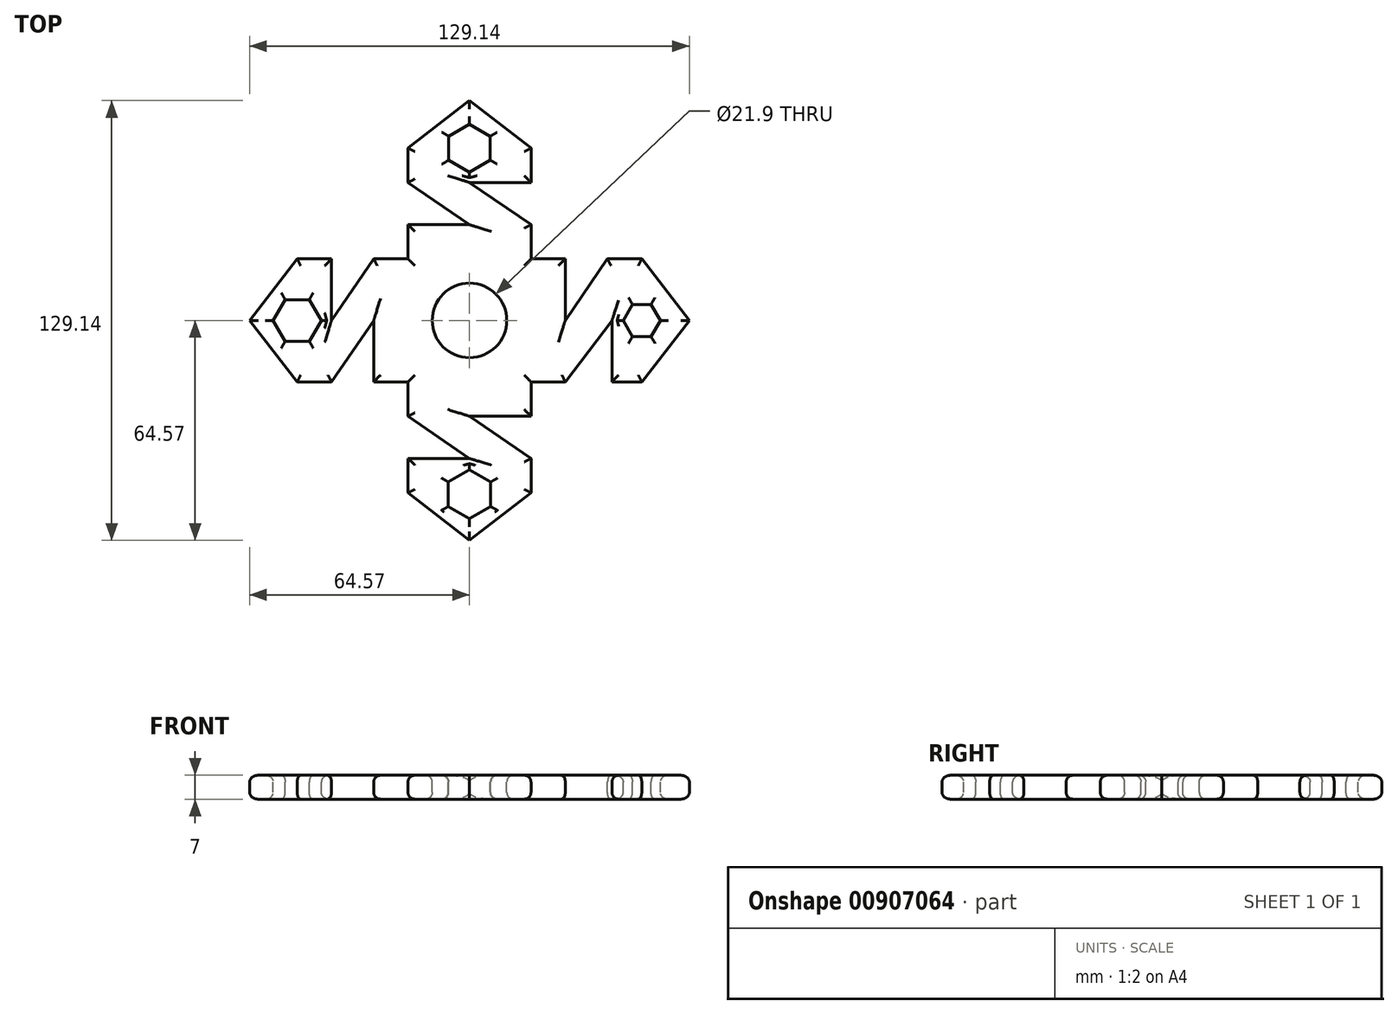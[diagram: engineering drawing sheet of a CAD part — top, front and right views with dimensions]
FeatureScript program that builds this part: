
annotation { "Feature Type Name" : "Feature", "Feature Type Description" : "" }
export const myFeature = defineFeature(function(context is Context, id is Id, definition is map)
    precondition{}
    {
        {
            var Q0;
            Q0=qCreatedBy(makeId("Top.planeOp"),FACE);
            var sketch = newSketch(context, id + "F0", { "sketchPlane" : qUnion([Q0])});
            skLineSegment(sketch, "E0", {"start": v(-18.07, 50.58) * mm, "end": v(0, 64.57) * mm});
            skLineSegment(sketch, "E1", {"start": v(18.07, 50.58) * mm, "end": v(0, 64.57) * mm});
            skLineSegment(sketch, "E2", {"start": v(0, 0) * mm, "end": v(-18.07, 18.07) * mm});
            skLineSegment(sketch, "E3", {"start": v(0, 0) * mm, "end": v(18.07, 18.07) * mm});
            skLineSegment(sketch, "E4", {"start": v(18.07, 18.07) * mm, "end": v(0, 0) * mm});
            skLineSegment(sketch, "E5", {"start": v(-18.07, 18.07) * mm, "end": v(-18.07, 28.12) * mm});
            skLineSegment(sketch, "E6", {"start": v(-18.07, 28.12) * mm, "end": v(-18.07, 18.07) * mm});
            skLineSegment(sketch, "E7", {"start": v(-18.07, 28.12) * mm, "end": v(0, 28.12) * mm});
            skLineSegment(sketch, "E8", {"start": v(18.07, 18.07) * mm, "end": v(18.07, 28.12) * mm});
            skLineSegment(sketch, "E9", {"start": v(-18.07, 50.58) * mm, "end": v(-18.07, 40.53) * mm});
            skLineSegment(sketch, "E10", {"start": v(18.07, 50.58) * mm, "end": v(18.07, 40.53) * mm});
            skLineSegment(sketch, "E11", {"start": v(0, 40.53) * mm, "end": v(18.07, 40.53) * mm});
            skLineSegment(sketch, "E12", {"start": v(0, 40.53) * mm, "end": v(18.07, 28.12) * mm});
            skLineSegment(sketch, "E13", {"start": v(-18.07, 40.53) * mm, "end": v(0, 28.12) * mm});
            skLineSegment(sketch, "E14", {"start": v(-50.58, -18.07) * mm, "end": v(-64.57, 0) * mm});
            skLineSegment(sketch, "E15", {"start": v(-50.58, 18.07) * mm, "end": v(-64.57, 0) * mm});
            skLineSegment(sketch, "E16", {"start": v(0, 0) * mm, "end": v(-18.07, -18.07) * mm});
            skLineSegment(sketch, "E17", {"start": v(-18.07, 18.07) * mm, "end": v(0, 0) * mm});
            skLineSegment(sketch, "E18", {"start": v(-18.07, -18.07) * mm, "end": v(-28.12, -18.07) * mm});
            skLineSegment(sketch, "E19", {"start": v(-28.12, -18.07) * mm, "end": v(-18.07, -18.07) * mm});
            skLineSegment(sketch, "E20", {"start": v(-28.12, -18.07) * mm, "end": v(-28.12, 0) * mm});
            skLineSegment(sketch, "E21", {"start": v(-18.07, 18.07) * mm, "end": v(-28.12, 18.07) * mm});
            skLineSegment(sketch, "E22", {"start": v(-50.58, -18.07) * mm, "end": v(-40.53, -18.07) * mm});
            skLineSegment(sketch, "E23", {"start": v(-50.58, 18.07) * mm, "end": v(-40.53, 18.07) * mm});
            skLineSegment(sketch, "E24", {"start": v(-40.53, 0) * mm, "end": v(-40.53, 18.07) * mm});
            skLineSegment(sketch, "E25", {"start": v(-40.53, 0) * mm, "end": v(-28.12, 18.07) * mm});
            skLineSegment(sketch, "E26", {"start": v(-40.53, -18.07) * mm, "end": v(-28.12, 0) * mm});
            skLineSegment(sketch, "E27", {"start": v(18.07, -50.58) * mm, "end": v(0, -64.57) * mm});
            skLineSegment(sketch, "E28", {"start": v(-18.07, -50.58) * mm, "end": v(0, -64.57) * mm});
            skLineSegment(sketch, "E29", {"start": v(0, 0) * mm, "end": v(18.07, -18.07) * mm});
            skLineSegment(sketch, "E30", {"start": v(-18.07, -18.07) * mm, "end": v(0, 0) * mm});
            skLineSegment(sketch, "E31", {"start": v(18.07, -18.07) * mm, "end": v(18.07, -28.12) * mm});
            skLineSegment(sketch, "E32", {"start": v(18.07, -28.12) * mm, "end": v(18.07, -18.07) * mm});
            skLineSegment(sketch, "E33", {"start": v(18.07, -28.12) * mm, "end": v(0, -28.12) * mm});
            skLineSegment(sketch, "E34", {"start": v(-18.07, -18.07) * mm, "end": v(-18.07, -28.12) * mm});
            skLineSegment(sketch, "E35", {"start": v(18.07, -50.58) * mm, "end": v(18.07, -40.53) * mm});
            skLineSegment(sketch, "E36", {"start": v(-18.07, -50.58) * mm, "end": v(-18.07, -40.53) * mm});
            skLineSegment(sketch, "E37", {"start": v(0, -40.53) * mm, "end": v(-18.07, -40.53) * mm});
            skLineSegment(sketch, "E38", {"start": v(0, -40.53) * mm, "end": v(-18.07, -28.12) * mm});
            skLineSegment(sketch, "E39", {"start": v(18.07, -40.53) * mm, "end": v(0, -28.12) * mm});
            skLineSegment(sketch, "E40", {"start": v(50.58, 18.07) * mm, "end": v(64.57, 0) * mm});
            skLineSegment(sketch, "E41", {"start": v(50.58, -18.07) * mm, "end": v(64.57, 0) * mm});
            skLineSegment(sketch, "E42", {"start": v(18.07, -18.07) * mm, "end": v(0, 0) * mm});
            skLineSegment(sketch, "E43", {"start": v(18.07, 18.07) * mm, "end": v(28.12, 18.07) * mm});
            skLineSegment(sketch, "E44", {"start": v(28.12, 18.07) * mm, "end": v(18.07, 18.07) * mm});
            skLineSegment(sketch, "E45", {"start": v(28.12, 18.07) * mm, "end": v(28.12, 0) * mm});
            skLineSegment(sketch, "E46", {"start": v(18.07, -18.07) * mm, "end": v(28.12, -18.07) * mm});
            skLineSegment(sketch, "E47", {"start": v(50.58, 18.07) * mm, "end": v(40.53, 18.07) * mm});
            skLineSegment(sketch, "E48", {"start": v(50.58, -18.07) * mm, "end": v(40.53, -18.07) * mm});
            skLineSegment(sketch, "E49", {"start": v(41.83, 0) * mm, "end": v(41.83, -18.07) * mm});
            skLineSegment(sketch, "E50", {"start": v(41.83, 0) * mm, "end": v(28.12, -18.07) * mm});
            skLineSegment(sketch, "E51", {"start": v(40.53, 18.07) * mm, "end": v(28.12, 0) * mm});
            skCircle(sketch, "E52", {"center": v(0, 0) * mm, "radius": 10.95 * mm});
            skCircle(sketch, "E53.cCircle", {"center": v(-50.58, 0) * mm, "radius": 7.06 * mm, "construction": true});
            skLineSegment(sketch, "E53.0", {"start": v(-43.53, 0) * mm, "end": v(-47.06, -6.11) * mm});
            skLineSegment(sketch, "E53.1", {"start": v(-47.06, -6.11) * mm, "end": v(-54.11, -6.11) * mm});
            skLineSegment(sketch, "E53.2", {"start": v(-54.11, -6.11) * mm, "end": v(-57.64, 0) * mm});
            skLineSegment(sketch, "E53.3", {"start": v(-57.64, 0) * mm, "end": v(-54.11, 6.11) * mm});
            skLineSegment(sketch, "E53.4", {"start": v(-54.11, 6.11) * mm, "end": v(-47.06, 6.11) * mm});
            skLineSegment(sketch, "E53.5", {"start": v(-47.06, 6.11) * mm, "end": v(-43.53, 0) * mm});
            skCircle(sketch, "E54.cCircle", {"center": v(50.58, 0) * mm, "radius": 5.45 * mm, "construction": true});
            skLineSegment(sketch, "E54.0", {"start": v(45.13, 0) * mm, "end": v(47.86, 4.72) * mm});
            skLineSegment(sketch, "E54.1", {"start": v(47.86, 4.72) * mm, "end": v(53.3, 4.72) * mm});
            skLineSegment(sketch, "E54.2", {"start": v(53.3, 4.72) * mm, "end": v(56.03, 0) * mm});
            skLineSegment(sketch, "E54.3", {"start": v(56.03, 0) * mm, "end": v(53.3, -4.72) * mm});
            skLineSegment(sketch, "E54.4", {"start": v(53.3, -4.72) * mm, "end": v(47.86, -4.72) * mm});
            skLineSegment(sketch, "E54.5", {"start": v(47.86, -4.72) * mm, "end": v(45.13, 0) * mm});
            skCircle(sketch, "E55.cCircle", {"center": v(0, 50.58) * mm, "radius": 7.04 * mm, "construction": true});
            skLineSegment(sketch, "E55.0", {"start": v(0, 43.54) * mm, "end": v(-6.1, 47.06) * mm});
            skLineSegment(sketch, "E55.1", {"start": v(-6.1, 47.06) * mm, "end": v(-6.1, 54.1) * mm});
            skLineSegment(sketch, "E55.2", {"start": v(-6.1, 54.1) * mm, "end": v(0, 57.63) * mm});
            skLineSegment(sketch, "E55.3", {"start": v(0, 57.63) * mm, "end": v(6.1, 54.1) * mm});
            skLineSegment(sketch, "E55.4", {"start": v(6.1, 54.1) * mm, "end": v(6.1, 47.06) * mm});
            skLineSegment(sketch, "E55.5", {"start": v(6.1, 47.06) * mm, "end": v(0, 43.54) * mm});
            skPoint(sketch, "E56.end.orphan", {"position": v(-18.07, 0) * mm});
            skPoint(sketch, "E57.end.orphan", {"position": v(18.07, 0) * mm});
            skPoint(sketch, "E58.end.orphan", {"position": v(0, -18.07) * mm});
            skPoint(sketch, "E59.end.orphan", {"position": v(0, 18.07) * mm});
            skCircle(sketch, "E60.cCircle", {"center": v(0, -51.04) * mm, "radius": 7.21 * mm, "construction": true});
            skLineSegment(sketch, "E60.0", {"start": v(0, -43.83) * mm, "end": v(6.25, -47.43) * mm});
            skLineSegment(sketch, "E60.1", {"start": v(6.25, -47.43) * mm, "end": v(6.25, -54.65) * mm});
            skLineSegment(sketch, "E60.2", {"start": v(6.25, -54.65) * mm, "end": v(0, -58.25) * mm});
            skLineSegment(sketch, "E60.3", {"start": v(0, -58.25) * mm, "end": v(-6.25, -54.65) * mm});
            skLineSegment(sketch, "E60.4", {"start": v(-6.25, -54.65) * mm, "end": v(-6.25, -47.43) * mm});
            skLineSegment(sketch, "E60.5", {"start": v(-6.25, -47.43) * mm, "end": v(0, -43.83) * mm});
            skSolve(sketch);
        }
        {
            var Q0;
            Q0 = qSketchRegion(id + "F0", true);
            extrude(context, id + "F1", {"entities" : qUnion([Q0]), "endBound" : BoundingType.SYMMETRIC, "oppositeDirection" : true, "depth" : 7 * mm, "offsetDistance" : 25 * mm});
        }
        {
            var Q0;
            Q0=makeQuery(id+"F1.opExtrude","CAP_FACE",FACE,{"disambiguationData":[OSD([sQuery(id+"F0.wireOp",EDGE,"E0"),sQuery(id+"F0.wireOp",EDGE,"E1"),sQuery(id+"F0.wireOp",EDGE,"E6"),sQuery(id+"F0.wireOp",EDGE,"E7"),sQuery(id+"F0.wireOp",EDGE,"E8"),sQuery(id+"F0.wireOp",EDGE,"E9"),sQuery(id+"F0.wireOp",EDGE,"E10"),sQuery(id+"F0.wireOp",EDGE,"E11"),sQuery(id+"F0.wireOp",EDGE,"E12"),sQuery(id+"F0.wireOp",EDGE,"E13"),sQuery(id+"F0.wireOp",EDGE,"E14"),sQuery(id+"F0.wireOp",EDGE,"E15"),sQuery(id+"F0.wireOp",EDGE,"E19"),sQuery(id+"F0.wireOp",EDGE,"E20"),sQuery(id+"F0.wireOp",EDGE,"E21"),sQuery(id+"F0.wireOp",EDGE,"E22"),sQuery(id+"F0.wireOp",EDGE,"E23"),sQuery(id+"F0.wireOp",EDGE,"E24"),sQuery(id+"F0.wireOp",EDGE,"E25"),sQuery(id+"F0.wireOp",EDGE,"E26"),sQuery(id+"F0.wireOp",EDGE,"E27"),sQuery(id+"F0.wireOp",EDGE,"E28"),sQuery(id+"F0.wireOp",EDGE,"E32"),sQuery(id+"F0.wireOp",EDGE,"E33"),sQuery(id+"F0.wireOp",EDGE,"E34"),sQuery(id+"F0.wireOp",EDGE,"E35"),sQuery(id+"F0.wireOp",EDGE,"E36"),sQuery(id+"F0.wireOp",EDGE,"E37"),sQuery(id+"F0.wireOp",EDGE,"E38"),sQuery(id+"F0.wireOp",EDGE,"E39"),sQuery(id+"F0.wireOp",EDGE,"E40"),sQuery(id+"F0.wireOp",EDGE,"E41"),sQuery(id+"F0.wireOp",EDGE,"E44"),sQuery(id+"F0.wireOp",EDGE,"E45"),sQuery(id+"F0.wireOp",EDGE,"E46"),sQuery(id+"F0.wireOp",EDGE,"E47"),sQuery(id+"F0.wireOp",EDGE,"E48"),sQuery(id+"F0.wireOp",EDGE,"E49"),sQuery(id+"F0.wireOp",EDGE,"E50"),sQuery(id+"F0.wireOp",EDGE,"E51")])],"isStart":true});
            var Q1;
            Q1=makeQuery(id+"F1.opExtrude","CAP_FACE",FACE,{"disambiguationData":[OSD([sQuery(id+"F0.wireOp",EDGE,"E0"),sQuery(id+"F0.wireOp",EDGE,"E1"),sQuery(id+"F0.wireOp",EDGE,"E6"),sQuery(id+"F0.wireOp",EDGE,"E7"),sQuery(id+"F0.wireOp",EDGE,"E8"),sQuery(id+"F0.wireOp",EDGE,"E9"),sQuery(id+"F0.wireOp",EDGE,"E10"),sQuery(id+"F0.wireOp",EDGE,"E11"),sQuery(id+"F0.wireOp",EDGE,"E12"),sQuery(id+"F0.wireOp",EDGE,"E13"),sQuery(id+"F0.wireOp",EDGE,"E14"),sQuery(id+"F0.wireOp",EDGE,"E15"),sQuery(id+"F0.wireOp",EDGE,"E19"),sQuery(id+"F0.wireOp",EDGE,"E20"),sQuery(id+"F0.wireOp",EDGE,"E21"),sQuery(id+"F0.wireOp",EDGE,"E22"),sQuery(id+"F0.wireOp",EDGE,"E23"),sQuery(id+"F0.wireOp",EDGE,"E24"),sQuery(id+"F0.wireOp",EDGE,"E25"),sQuery(id+"F0.wireOp",EDGE,"E26"),sQuery(id+"F0.wireOp",EDGE,"E27"),sQuery(id+"F0.wireOp",EDGE,"E28"),sQuery(id+"F0.wireOp",EDGE,"E32"),sQuery(id+"F0.wireOp",EDGE,"E33"),sQuery(id+"F0.wireOp",EDGE,"E34"),sQuery(id+"F0.wireOp",EDGE,"E35"),sQuery(id+"F0.wireOp",EDGE,"E36"),sQuery(id+"F0.wireOp",EDGE,"E37"),sQuery(id+"F0.wireOp",EDGE,"E38"),sQuery(id+"F0.wireOp",EDGE,"E39"),sQuery(id+"F0.wireOp",EDGE,"E40"),sQuery(id+"F0.wireOp",EDGE,"E41"),sQuery(id+"F0.wireOp",EDGE,"E44"),sQuery(id+"F0.wireOp",EDGE,"E45"),sQuery(id+"F0.wireOp",EDGE,"E46"),sQuery(id+"F0.wireOp",EDGE,"E47"),sQuery(id+"F0.wireOp",EDGE,"E48"),sQuery(id+"F0.wireOp",EDGE,"E49"),sQuery(id+"F0.wireOp",EDGE,"E50"),sQuery(id+"F0.wireOp",EDGE,"E51")])],"isStart":false});
            fillet(context, id + "F2", {"entities" : qUnion([Q0, Q1]), "radius" : 2 * mm, "tangentPropagation" : true, "allowEdgeOverflow" : false});
        }
    });
